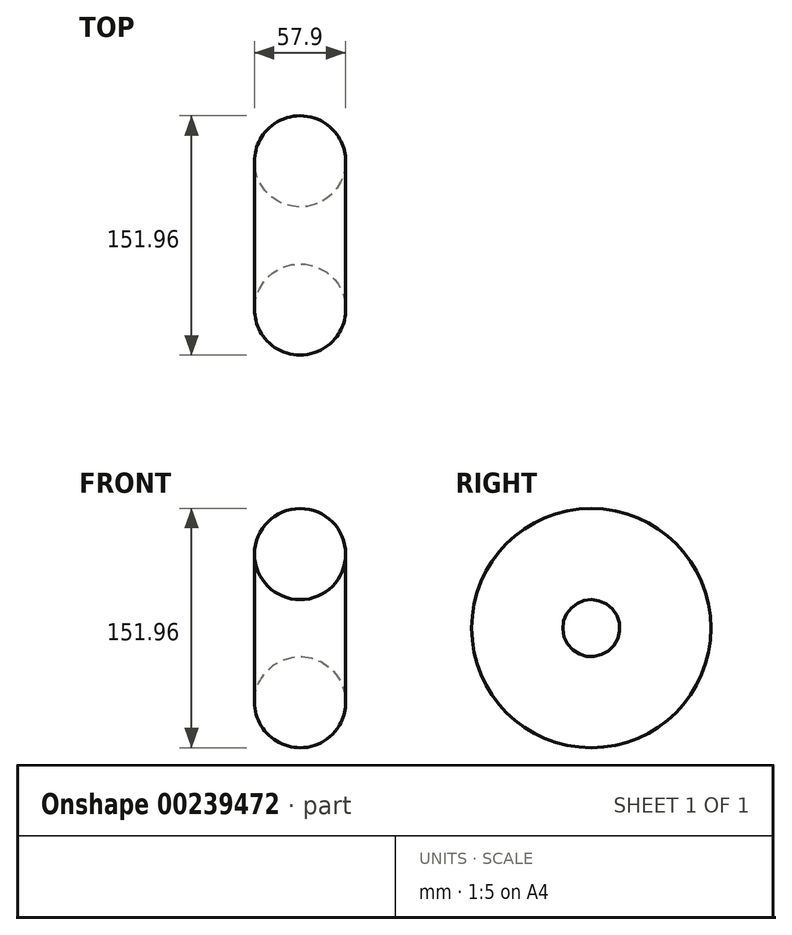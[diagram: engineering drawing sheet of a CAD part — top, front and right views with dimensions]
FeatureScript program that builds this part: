
annotation { "Feature Type Name" : "Feature", "Feature Type Description" : "" }
export const myFeature = defineFeature(function(context is Context, id is Id, definition is map)
    precondition{}
    {
        {
            var Q0;
            Q0=qCreatedBy(makeId("Top.planeOp"),FACE);
            var sketch = newSketch(context, id + "F0", { "sketchPlane" : qUnion([Q0])});
            skCircle(sketch, "E0", {"center": v(-54.16, -47.03) * mm, "radius": 28.95 * mm});
            skLineSegment(sketch, "E1", {"start": v(-75.7, 0) * mm, "end": v(75.7, 0) * mm, "construction": true});
            skSolve(sketch);
        }
        {
            var Q0;
            Q0 = qSketchRegion(id + "F0", true);
            var Q1;
            Q1=sQuery(id+"F0.wireOp",EDGE,"E1");
            revolve(context, id + "F1", {"entities" : qUnion([Q0]), "axis" : qUnion([Q1]), "revolveType" : RevolveType.FULL});
        }
    });
